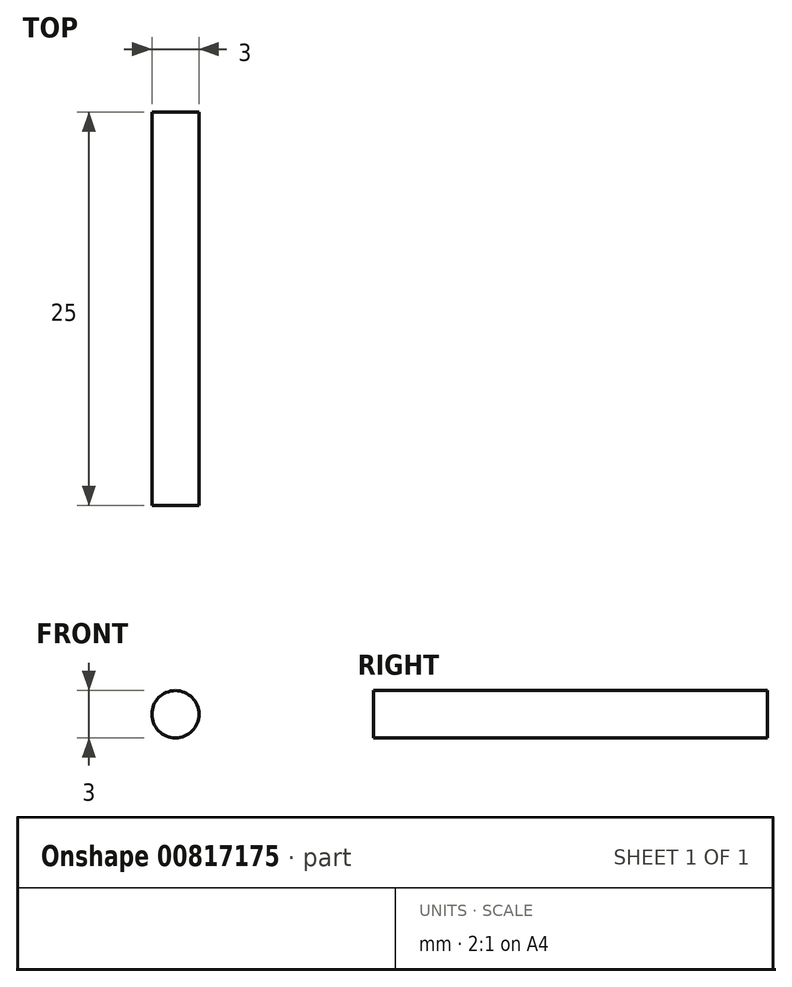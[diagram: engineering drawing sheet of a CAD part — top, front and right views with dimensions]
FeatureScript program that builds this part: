
annotation { "Feature Type Name" : "Feature", "Feature Type Description" : "" }
export const myFeature = defineFeature(function(context is Context, id is Id, definition is map)
    precondition{}
    {
        {
            var Q0;
            Q0=qCreatedBy(makeId("Front.planeOp"),FACE);
            var sketch = newSketch(context, id + "F0", { "sketchPlane" : qUnion([Q0])});
            skCircle(sketch, "E0", {"center": v(0, 0) * mm, "radius": 1.5 * mm});
            skSolve(sketch);
        }
        {
            var Q0;
            Q0 = qSketchRegion(id + "F0", true);
            extrude(context, id + "F1", {"entities" : qUnion([Q0]), "endBound" : BoundingType.SYMMETRIC, "depth" : 25 * mm, "offsetDistance" : 25 * mm});
        }
    });
